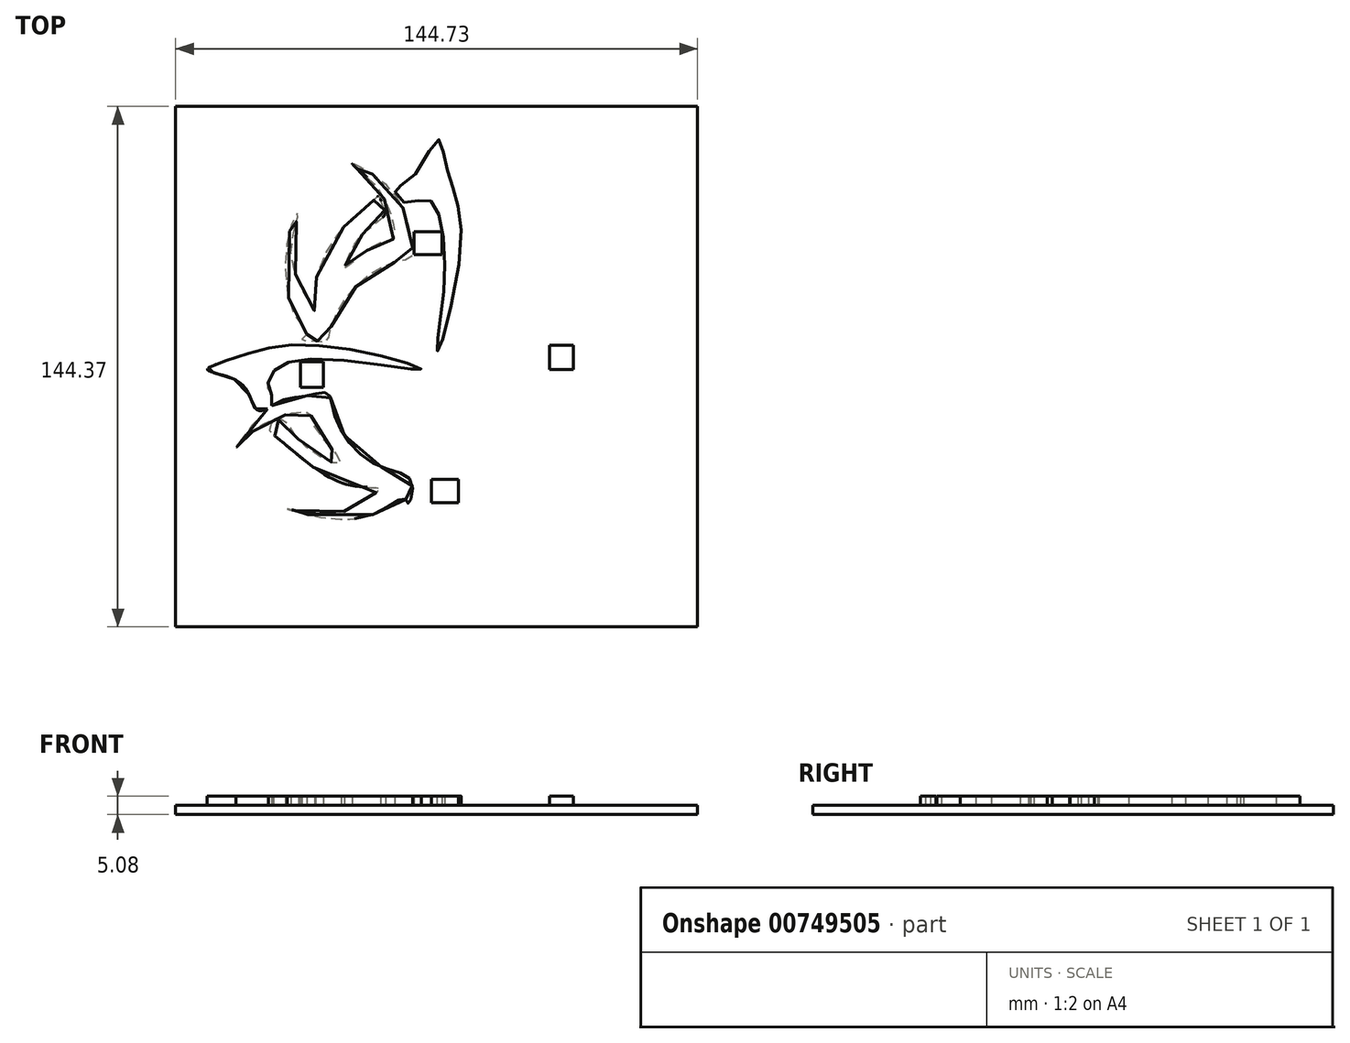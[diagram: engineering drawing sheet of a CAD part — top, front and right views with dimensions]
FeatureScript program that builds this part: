
annotation { "Feature Type Name" : "Feature", "Feature Type Description" : "" }
export const myFeature = defineFeature(function(context is Context, id is Id, definition is map)
    precondition{}
    {
        {
            var Q0;
            Q0=qCreatedBy(makeId("Top.planeOp"),FACE);
            var sketch = newSketch(context, id + "F0", { "sketchPlane" : qUnion([Q0])});
            skLineSegment(sketch, "E0.bottom", {"start": v(-72.74, 73) * mm, "end": v(71.99, 73) * mm});
            skLineSegment(sketch, "E0.top", {"start": v(-72.74, -71.38) * mm, "end": v(71.99, -71.38) * mm});
            skLineSegment(sketch, "E0.left", {"start": v(-72.74, 73) * mm, "end": v(-72.74, -71.38) * mm});
            skLineSegment(sketch, "E0.right", {"start": v(71.99, 73) * mm, "end": v(71.99, -71.38) * mm});
            skSolve(sketch);
        }
        {
            var Q0;
            Q0=makeQuery(id+"F0.imprint","IMPRINT",FACE,{"disambiguationData":[TD([[makeQuery(id+"F0.imprint","IMPRINT",EDGE,{"derivedFrom":sQuery(id+"F0.wireOp",EDGE,"E0.bottom")}),-1.0]])]});
            extrude(context, id + "F1", {"entities" : qUnion([Q0]), "depth" : 2.54 * mm, "offsetDistance" : 25.4 * mm});
        }
        {
            var Q0;
            Q0=qCreatedBy(makeId("Top.planeOp"),FACE);
            cPlane(context, id + "F2", {"entities" : qUnion([Q0]), "cplaneType" : CPlaneType.OFFSET, "offset" : 2.54 * mm, "width" : 152.4 * mm, "height" : 152.4 * mm});
        }
        {
            var Q0;
            Q0=qCreatedBy(id+"F2.planeOp",FACE);
            var sketch = newSketch(context, id + "F3", { "sketchPlane" : qUnion([Q0])});
            skFitSpline(sketch, "E1", {"points": [v(-36.39, 9.8) * mm, v(-37.78, 8.2) * mm, v(-33.9, 8) * mm, v(-30.88, 7.76) * mm, v(-29.64, 11.74) * mm, v(-23.29, 22.54) * mm, v(-13.02, 29.47) * mm, v(-7.34, 31.34) * mm, v(-7.12, 34.39) * mm, v(-9.28, 44) * mm, v(-16.56, 53.08) * mm, v(-23.72, 57.18) * mm, v(-21.19, 54.73) * mm, v(-14.64, 46.91) * mm, v(-12.2, 36.45) * mm, v(-14.09, 35.68) * mm, v(-19.91, 32.93) * mm, v(-25.83, 28.23) * mm, v(-25.12, 30.44) * mm, v(-21.28, 37.18) * mm, v(-14.6, 43.23) * mm, v(-15.16, 45.15) * mm, v(-16.44, 48.1) * mm, v(-18.26, 46.47) * mm, v(-25.56, 40.16) * mm, v(-33.92, 24.04) * mm, v(-34.03, 16.23) * mm, v(-35.96, 19.36) * mm, v(-40.76, 32.92) * mm, v(-38.68, 43.45) * mm, v(-41.14, 38.53) * mm, v(-39.75, 15) * mm, v(-36.39, 9.8) * mm]});
            skSolve(sketch);
        }
        {
            var Q0;
            Q0=makeQuery(id+"F3.imprint","IMPRINT",FACE,{"disambiguationData":[TD([[makeQuery(id+"F3.imprint","IMPRINT",EDGE,{"derivedFrom":sQuery(id+"F3.wireOp",EDGE,"E1")}),1.0]])]});
            extrude(context, id + "F4", {"entities" : qUnion([Q0]), "operationType" : NewBodyOperationType.ADD, "depth" : 2.54 * mm, "offsetDistance" : 25.4 * mm});
        }
        {
            var Q0;
            Q0=qCreatedBy(id+"F2.planeOp",FACE);
            var sketch = newSketch(context, id + "F5", { "sketchPlane" : qUnion([Q0])});
            skLineSegment(sketch, "E2.bottom", {"start": v(-38.16, 2.18) * mm, "end": v(-31.73, 2.18) * mm});
            skLineSegment(sketch, "E2.top", {"start": v(-38.16, -4.98) * mm, "end": v(-31.73, -4.98) * mm});
            skLineSegment(sketch, "E2.left", {"start": v(-38.16, 2.18) * mm, "end": v(-38.16, -4.98) * mm});
            skLineSegment(sketch, "E2.right", {"start": v(-31.73, 2.18) * mm, "end": v(-31.73, -4.98) * mm});
            skSolve(sketch);
        }
        {
            var Q0;
            Q0=qCreatedBy(id+"F2.planeOp",FACE);
            var sketch = newSketch(context, id + "F6", { "sketchPlane" : qUnion([Q0])});
            skLineSegment(sketch, "E3.bottom", {"start": v(-6.6, 38.2) * mm, "end": v(1.18, 38.2) * mm});
            skLineSegment(sketch, "E3.top", {"start": v(-6.6, 31.95) * mm, "end": v(1.18, 31.95) * mm});
            skLineSegment(sketch, "E3.left", {"start": v(-6.6, 38.2) * mm, "end": v(-6.6, 31.95) * mm});
            skLineSegment(sketch, "E3.right", {"start": v(1.18, 38.2) * mm, "end": v(1.18, 31.95) * mm});
            skSolve(sketch);
        }
        {
            var Q0;
            Q0=qCreatedBy(id+"F2.planeOp",FACE);
            var sketch = newSketch(context, id + "F7", { "sketchPlane" : qUnion([Q0])});
            skLineSegment(sketch, "E4.bottom", {"start": v(-1.77, -30.49) * mm, "end": v(5.65, -30.49) * mm});
            skLineSegment(sketch, "E4.top", {"start": v(-1.77, -36.9) * mm, "end": v(5.65, -36.9) * mm});
            skLineSegment(sketch, "E4.left", {"start": v(-1.77, -30.49) * mm, "end": v(-1.77, -36.9) * mm});
            skLineSegment(sketch, "E4.right", {"start": v(5.65, -30.49) * mm, "end": v(5.65, -36.9) * mm});
            skSolve(sketch);
        }
        {
            var Q0;
            Q0=makeQuery(id+"F6.imprint","IMPRINT",FACE,{"disambiguationData":[TD([[makeQuery(id+"F6.imprint","IMPRINT",EDGE,{"derivedFrom":sQuery(id+"F6.wireOp",EDGE,"E3.bottom")}),-1.0]])]});
            extrude(context, id + "F8", {"entities" : qUnion([Q0]), "operationType" : NewBodyOperationType.ADD, "depth" : 2.54 * mm, "offsetDistance" : 25.4 * mm});
        }
        {
            var Q0;
            Q0=makeQuery(id+"F5.imprint","IMPRINT",FACE,{"disambiguationData":[TD([[makeQuery(id+"F5.imprint","IMPRINT",EDGE,{"derivedFrom":sQuery(id+"F5.wireOp",EDGE,"E2.bottom")}),-1.0]])]});
            extrude(context, id + "F9", {"entities" : qUnion([Q0]), "operationType" : NewBodyOperationType.ADD, "depth" : 2.54 * mm, "offsetDistance" : 25.4 * mm});
        }
        {
            var Q0;
            Q0=makeQuery(id+"F7.imprint","IMPRINT",FACE,{"disambiguationData":[TD([[makeQuery(id+"F7.imprint","IMPRINT",EDGE,{"derivedFrom":sQuery(id+"F7.wireOp",EDGE,"E4.bottom")}),-1.0]])]});
            extrude(context, id + "F10", {"entities" : qUnion([Q0]), "operationType" : NewBodyOperationType.ADD, "depth" : 2.54 * mm, "offsetDistance" : 25.4 * mm});
        }
        {
            var Q0;
            Q0=qCreatedBy(id+"F2.planeOp",FACE);
            var sketch = newSketch(context, id + "F11", { "sketchPlane" : qUnion([Q0])});
            skLineSegment(sketch, "E5.bottom", {"start": v(30.93, 6.77) * mm, "end": v(37.53, 6.77) * mm});
            skLineSegment(sketch, "E5.top", {"start": v(30.93, 0) * mm, "end": v(37.53, 0) * mm});
            skLineSegment(sketch, "E5.left", {"start": v(30.93, 6.77) * mm, "end": v(30.93, 0) * mm});
            skLineSegment(sketch, "E5.right", {"start": v(37.53, 6.77) * mm, "end": v(37.53, 0) * mm});
            skSolve(sketch);
        }
        {
            var Q0;
            Q0=makeQuery(id+"F11.imprint","IMPRINT",FACE,{"disambiguationData":[TD([[makeQuery(id+"F11.imprint","IMPRINT",EDGE,{"derivedFrom":sQuery(id+"F11.wireOp",EDGE,"E5.bottom")}),-1.0]])]});
            extrude(context, id + "F12", {"entities" : qUnion([Q0]), "operationType" : NewBodyOperationType.ADD, "depth" : 2.54 * mm, "offsetDistance" : 25.4 * mm});
        }
        {
            var Q0;
            Q0=qCreatedBy(id+"F2.planeOp",FACE);
            var sketch = newSketch(context, id + "F13", { "sketchPlane" : qUnion([Q0])});
            skFitSpline(sketch, "E6", {"points": [v(-7.3, -31.23) * mm, v(-17.54, -26.23) * mm, v(-28.54, -12.93) * mm, v(-30.64, -6.6) * mm, v(-36.44, -7.27) * mm, v(-46.58, -10.42) * mm, v(-55.96, -21.86) * mm, v(-52.32, -18.01) * mm, v(-44.21, -13.22) * mm, v(-35.79, -11.8) * mm, v(-34.43, -15.52) * mm, v(-26.84, -25.68) * mm, v(-29.34, -25.75) * mm, v(-39.19, -18.74) * mm, v(-43.1, -13.85) * mm, v(-46.93, -15.87) * mm, v(-43.65, -19.68) * mm, v(-25.77, -31.68) * mm, v(-15.94, -33.02) * mm, v(-18.53, -35) * mm, v(-30.01, -40.1) * mm, v(-41.76, -38.67) * mm, v(-21.22, -41.11) * mm, v(-9.16, -35.85) * mm, v(-8.16, -37.14) * mm, v(-7.3, -31.23) * mm]});
            skSolve(sketch);
        }
        {
            var Q0;
            Q0=makeQuery(id+"F13.imprint","IMPRINT",FACE,{"disambiguationData":[TD([[makeQuery(id+"F13.imprint","IMPRINT",EDGE,{"derivedFrom":sQuery(id+"F13.wireOp",EDGE,"E6")}),1.0]])]});
            extrude(context, id + "F14", {"entities" : qUnion([Q0]), "operationType" : NewBodyOperationType.ADD, "depth" : 2.54 * mm, "offsetDistance" : 25.4 * mm});
        }
        {
            var Q0;
            Q0=qCreatedBy(id+"F2.planeOp",FACE);
            var sketch = newSketch(context, id + "F15", { "sketchPlane" : qUnion([Q0])});
            skFitSpline(sketch, "E7", {"points": [v(-49.9, -11.32) * mm, v(-45.64, -9.32) * mm, v(-47.1, -5.04) * mm, v(-45.04, 0) * mm, v(-31.22, 2.93) * mm, v(-4.7, 0) * mm, v(-12.7, 3.03) * mm, v(-40.08, 6.9) * mm, v(-55.25, 3.63) * mm, v(-63.94, 0) * mm, v(-54.45, -3.98) * mm, v(-49.9, -11.32) * mm]});
            skSolve(sketch);
        }
        {
            var Q0;
            Q0=makeQuery(id+"F15.imprint","IMPRINT",FACE,{"disambiguationData":[TD([[makeQuery(id+"F15.imprint","IMPRINT",EDGE,{"derivedFrom":sQuery(id+"F15.wireOp",EDGE,"E7")}),1.0]])]});
            extrude(context, id + "F16", {"entities" : qUnion([Q0]), "operationType" : NewBodyOperationType.ADD, "depth" : 2.54 * mm, "offsetDistance" : 25.4 * mm});
        }
        {
            var Q0;
            Q0=qCreatedBy(id+"F2.planeOp",FACE);
            var sketch = newSketch(context, id + "F17", { "sketchPlane" : qUnion([Q0])});
            skFitSpline(sketch, "E8", {"points": [v(-9.39, 46.36) * mm, v(-11.85, 50.17) * mm, v(-7.89, 52.32) * mm, v(0, 63.79) * mm, v(1.76, 59.25) * mm, v(4.26, 50.04) * mm, v(6.38, 34.22) * mm, v(0, 5.1) * mm, v(0, 9.37) * mm, v(1.88, 25.79) * mm, v(0, 43.86) * mm, v(-3.42, 47.28) * mm, v(-9.39, 46.36) * mm]});
            skSolve(sketch);
        }
        {
            var Q0;
            Q0=makeQuery(id+"F17.imprint","IMPRINT",FACE,{"disambiguationData":[TD([[makeQuery(id+"F17.imprint","IMPRINT",EDGE,{"derivedFrom":sQuery(id+"F17.wireOp",EDGE,"E8")}),-1.0]])]});
            extrude(context, id + "F18", {"entities" : qUnion([Q0]), "operationType" : NewBodyOperationType.ADD, "depth" : 2.54 * mm, "offsetDistance" : 25.4 * mm});
        }
    });
